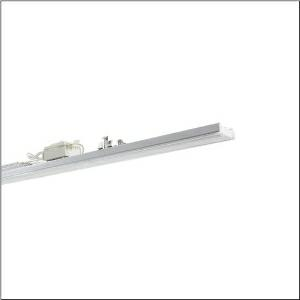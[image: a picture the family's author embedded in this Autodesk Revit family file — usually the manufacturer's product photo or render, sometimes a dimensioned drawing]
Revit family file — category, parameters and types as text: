
# Revit family: licross_r__21_recessed_ho_52tl12dv4l2m3s4_342f
name_source: partatom
category: Lighting Fixtures
units: mm (PartAtom-declared; Revit-internal decimal feet)

## family parameters
Cut with Voids When Loaded = No
Host = Face
Light Source = No
Part Type = Normal
Room Calculation Point = No
Round Connector Dimension = Use Diameter
Shared = No

## types (1)
- --- (1 x LED, 910 lm, 6.4 W, 4000K)
    Apparent Load = 6 VA
    CIE Flux Codes = 69 91 98 100 100
    Color Rendering = 80
    Color Temperature = 4000K
    Default Elevation = 1800 mm
    Description = Licross® 21 Recessed HO, luminaire insert, of sheet steel, galvanised, coil coated, white, length: 2.250mm, width: 66mm, height: 67mm, LED rated luminous flux: 22.710lm, light colour: 840, control gear: DALI 2, with plug, 6-pole, with phase selection, for trunking rail, 9 or 11-core, mains connection: 220..240V, AC, 50/60Hz, rated input power: 129W, for trunking rail, 9-/11-core, halogen-free wiring, for emergency light function, converter,control gear: single battery element, battery: LiFePO4, 9Ah, primary optical cover: cover, of PMMA, light emission: direct distribution, primary light characteristic: symmetric, protection rating (complete): IP40, insulation class (complete): insulation class I (protective earthing), certification: CE, UKCA, protection symbol: D if used in an environment without relevant dust loads with corresponding accessories, impact resistance: IK06, permissible ambient temperature for indoor applications: +5..+30°C, standard: EN 60598-2-22, LABS conformity tested according to VDMA 24364:2018-05, reducing of maximum allowable ambient temperature of 5°C with ceiling mounting, corresponds to IFS (International Featured Standards) requirements for safety and quality in the food industry, packaging unit: 1 piece
    Height = 58 mm
    Lamp = 1 x LED
    Lamp Light Flux = 910 lm
    Lamp Power = 6.4 W
    Lamp count = 1
    Length = 2250 mm
    Luminous efficacy = 142 lm/W
    Manufacturer = Siteco
    ModVariant = No
    Model = 52TL12DV4L2M3S4
    Mounting Place = Ceiling
    Mounting Type = Pendant
    Number of Poles = 1
    OnlyDefault = Yes
    Power Factor = 1
    Product Name = Licross® 21 Recessed HO
    Product group = luminaire insert
    ProductGroupID = 902
    Protection Class = Protection class I
    Protection Degree = IP 40
    RLX_Detail_Level = 1
    RLX_Emergency_Light_Flux = 0 lm
    RLX_Emergency_Type = 0
    RLX_Emergency_Type_DB = No
    RlxData = <blob elided: 29929 chars, md5=b223a141>
    Socket = socket
    Standby Power = 0 W
    System Light Flux = 910 lm
    System Power = 6 W
    Type Comments = : emergency light operation: 3 h
    Type Image = l_1296930.jpg
    URL = http://relux.com
    VarID = @adj_109328
    Voltage = 0 V
    Weight = 0.00 kg
    Width = 66 mm

## geometry (parser evidence)
native form markers: Blend x4, Sweep x9
no freeform markers — native parametric forms only
